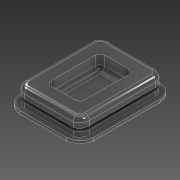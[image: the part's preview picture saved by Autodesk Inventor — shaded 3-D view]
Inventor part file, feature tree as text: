
AUTODESK INVENTOR PART (.ipt)
format: ipt  version: 2021 (Build 250183000, 183)  size: 385,536 bytes
history: native  units: mm
features: extrude x6, sketch x5, fillet x4, projected_geometry x3, other x1
ambient origin geometry x8: Origin, YZ Plane, XZ Plane, XY Plane, X Axis, Y Axis, Z Axis, Center Point
bodies: Body1 (feature_tree)
feature tree (19):
  other  "Sólido1"
  sketch  "Boceto1"  dims[d0=27.85mm d1=40.5mm]
  extrude  "Extrusión1"  Depth=40.5mm
  extrude  "Extrusión2"  Depth=2.0mm
  extrude  "Extrusión3"  Depth=2.0mm
  extrude  "Extrusión4"  Depth=2.0mm
  extrude  "Extrusión5"  Depth=0.5mm TaperAngle=0.0deg
  fillet  "Empalme1"  Radius=2.0mm
  fillet  "Empalme2"  Radius=1.5mm
  fillet  "Empalme3"  Radius=1.3mm
  extrude  "Extrusión6"  Depth=0.5mm TaperAngle=0.0deg
  fillet  "Empalme4"  Radius=1.8mm
  sketch  "Boceto2"  dims[d2=6.0mm d3=2.0mm]
  projected_geometry  "Contorno proyectado1"
  sketch  "Boceto3"  dims[d4=2.0mm d5=2.0mm]
  projected_geometry  "Contorno proyectado2"
  sketch  "Boceto4"  dims[d6=2.0mm d7=2.0mm]
  projected_geometry  "Contorno proyectado3"
  sketch  "Boceto5"  dims[d8=0.4mm d9=4.0mm d10=0.0mm d11=2.0mm d12=0.0mm d13=1.5mm d14=1.3mm d15=0.0mm d16=4.0mm d17=0.0mm d18=1.8mm d19=2.0mm d20=6.0mm d21=0.0mm d22=2.0mm d23=2.0mm d24=1.0mm d25=0.3mm d26=0.0mm d27=0.5mm d28=0.872665mm]
